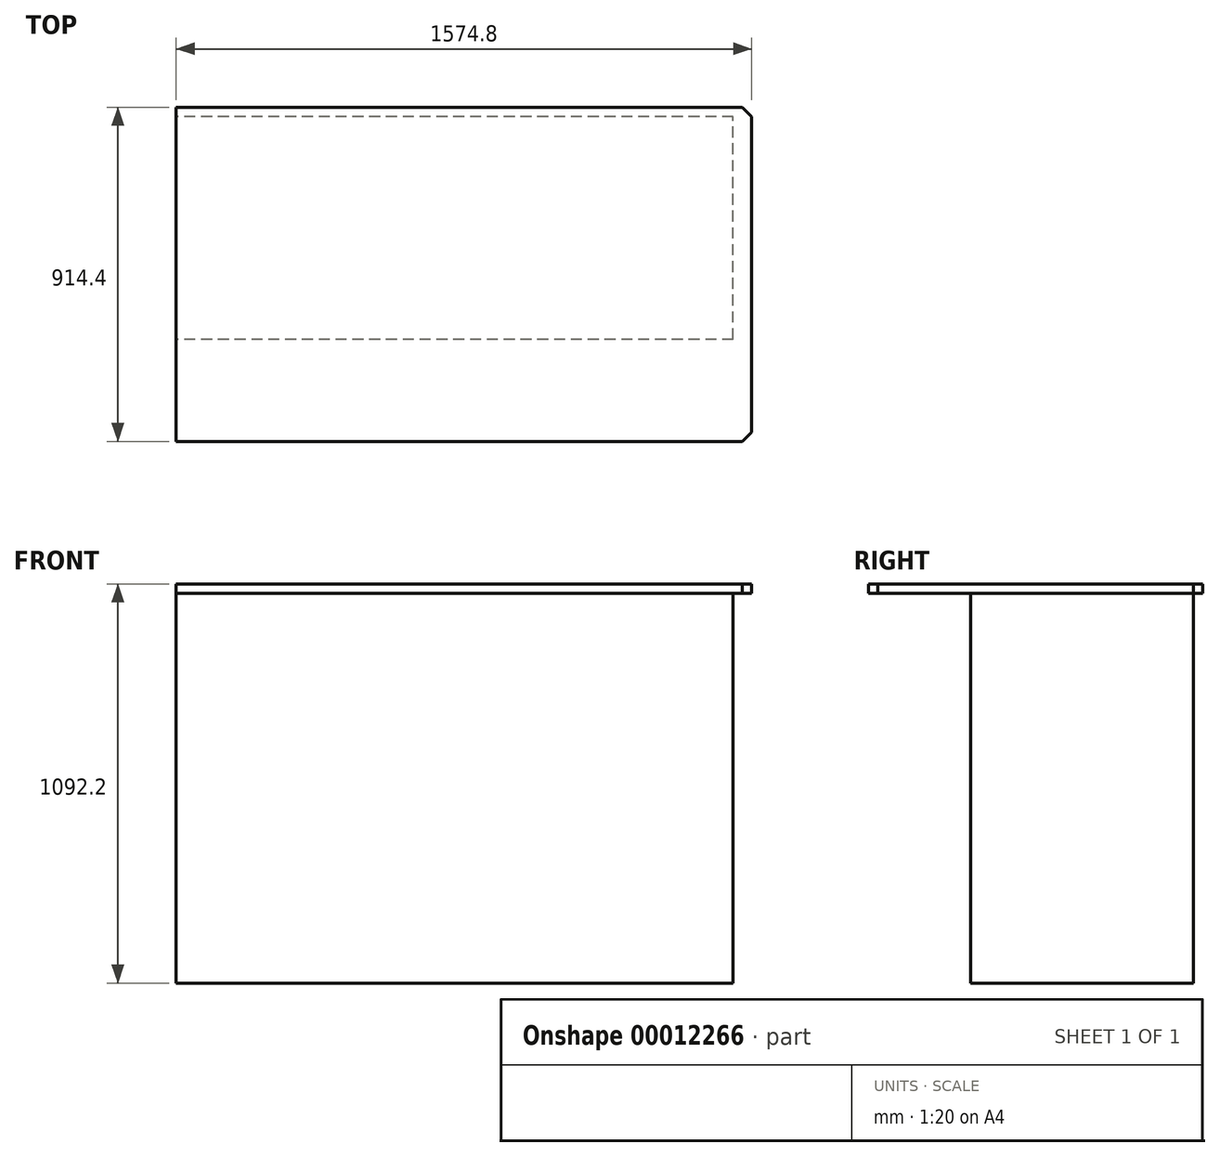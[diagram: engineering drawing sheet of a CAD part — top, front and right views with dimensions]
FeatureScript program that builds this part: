
annotation { "Feature Type Name" : "Feature", "Feature Type Description" : "" }
export const myFeature = defineFeature(function(context is Context, id is Id, definition is map)
    precondition{}
    {
        {
            var Q0;
            Q0=qCreatedBy(makeId("Top.planeOp"),FACE);
            cPlane(context, id + "F0", {"entities" : qUnion([Q0]), "cplaneType" : CPlaneType.OFFSET, "offset" : 1066.8 * mm, "width" : 152.4 * mm, "height" : 152.4 * mm});
        }
        {
            var Q0;
            Q0=qCreatedBy(id+"F0.planeOp",FACE);
            var sketch = newSketch(context, id + "F1", { "sketchPlane" : qUnion([Q0])});
            skLineSegment(sketch, "E0.bottom", {"start": v(0, 0) * mm, "end": v(1524, 0) * mm});
            skLineSegment(sketch, "E0.top", {"start": v(0, -609.6) * mm, "end": v(1524, -609.6) * mm});
            skLineSegment(sketch, "E0.left", {"start": v(0, 0) * mm, "end": v(0, -609.6) * mm});
            skLineSegment(sketch, "E0.right", {"start": v(1524, 0) * mm, "end": v(1524, -609.6) * mm});
            skLineSegment(sketch, "E1.bottom", {"start": v(0, 25.4) * mm, "end": v(1574.8, 25.4) * mm});
            skLineSegment(sketch, "E1.top", {"start": v(0, -889) * mm, "end": v(1574.8, -889) * mm});
            skLineSegment(sketch, "E1.left", {"start": v(0, 25.4) * mm, "end": v(0, -889) * mm});
            skLineSegment(sketch, "E1.right", {"start": v(1574.8, 25.4) * mm, "end": v(1574.8, -889) * mm});
            skSolve(sketch);
        }
        {
            var Q0;
            {var subQ2=sQuery(id+"F1.wireOp",EDGE,"E0.bottom");Q0=makeQuery(id+"F1.imprint","IMPRINT",FACE,{"disambiguationData":[TD([[makeQuery(id+"F1.imprint","IMPRINT",EDGE,{"derivedFrom":subQ2}),-1.0]])]});}
            var Q1;
            Q1=qCreatedBy(makeId("Top.planeOp"),FACE);
            extrude(context, id + "F2", {"entities" : qUnion([Q0]), "endBound" : BoundingType.UP_TO_SURFACE, "oppositeDirection" : true, "endBoundEntityFace" : qUnion([Q1]), "depth" : 25.4 * mm});
        }
        {
            var Q0;
            Q0 = qSketchRegion(id + "F1", true);
            extrude(context, id + "F3", {"entities" : qUnion([Q0]), "depth" : 25.4 * mm});
        }
        {
            var Q0;
            Q0=makeQuery(id+"F3.opExtrude","SWEPT_EDGE",EDGE,{"disambiguationData":[OSD([sQuery(id+"F1.wireOp",EDGE,"E1.top"),sQuery(id+"F1.wireOp",EDGE,"E1.right")])]});
            var Q1;
            Q1=makeQuery(id+"F3.opExtrude","SWEPT_EDGE",EDGE,{"disambiguationData":[OSD([sQuery(id+"F1.wireOp",EDGE,"E1.bottom"),sQuery(id+"F1.wireOp",EDGE,"E1.right")])]});
            chamfer(context, id + "F4", {"entities" : qUnion([Q0, Q1]), "width" : 25.4 * mm, "tangentPropagation" : true});
        }
    });
